# Revit family: DLB040003-V2
name_source: partatom
category: Modèles génériques
revit_build: Autodesk Revit 2015 (Build: 20140606_1530(x64)
units: mm (PartAtom-declared; Revit-internal decimal feet)

## types (1)
- Type 1
    Category = Shower mixer
    Commentaires du type = Recessed time flow mixer
    Description = French manufacturer Delabie is a leader in the European sanitary ware market for non-domestic places. Water controls, solutions for disabled people, sanitary ware, for schools, leisure centres, offices, hospitals, airports…
    Fabricant = DELABIE
    Features  = Recessed time flow shower mixer:
Waterproof recessing housing.
Tamperproof polished stainless steel wall plate 160 x 220mm.
A 10 to 30mm allowance for different wall finishes.
TEMPOMIX ¾" single control mixer.
Ligature-resistant ring.
Temperature control and operation on the push-button.
Maximum temperature limiter (adjustable by the installer).
Time flow 30 sec., soft-touch operation.
Flow rate 12 lpm at 3 bar.
Concealed fixings, stopcocks M½".
Integrated non-return valves and filters.
Chrome-plated metal control.
10-year warranty.
    Finish = DLB040003 1
    FlowRate lpm = 12 lpm at 3 bar
    FlowRate lps = 0,20 lps at 3 bar
    Grade = ACS - PZH
    IntegralAccessory = Stopcocks
    IntegralAccessoryOptions = Thermostatic mixing valve
    ManufacturerName = DELABIE
    ManufacturerURL = http://www.delabie.com
    Material = Stainless steel
    ModelNumber = 790BOX+790218
    Modèle = TEMPOMIX
    Name = TEMPOMIX
    NominalHeight = 160 mm  [stored 0.524934 ft]
    NominalWidth = 220 mm  [stored 0.721785 ft]
    Operation = Time flow mixer
    ProductInformation = http://www.delabie.com
    Radius = 10 mm  [stored 0.0328084 ft]
    SerialNumber = 3456330139960 + 3456330140331
    URL = http://www.delabie.com
    Version = v2
    WarrantyDescription = Any manufacturing defect
    WarrantyDurationUnit = 10 years
    WaterSupplyTemperatureMaximum = 55°C-85° (∆50°C : CW/HW)

note: [stored X ft] marks values corroborated as IEEE doubles in the binary element streams (Revit-internal decimal feet)

## geometry (parser evidence)
native form markers: Blend x26, Sweep x6
no freeform markers — native parametric forms only
